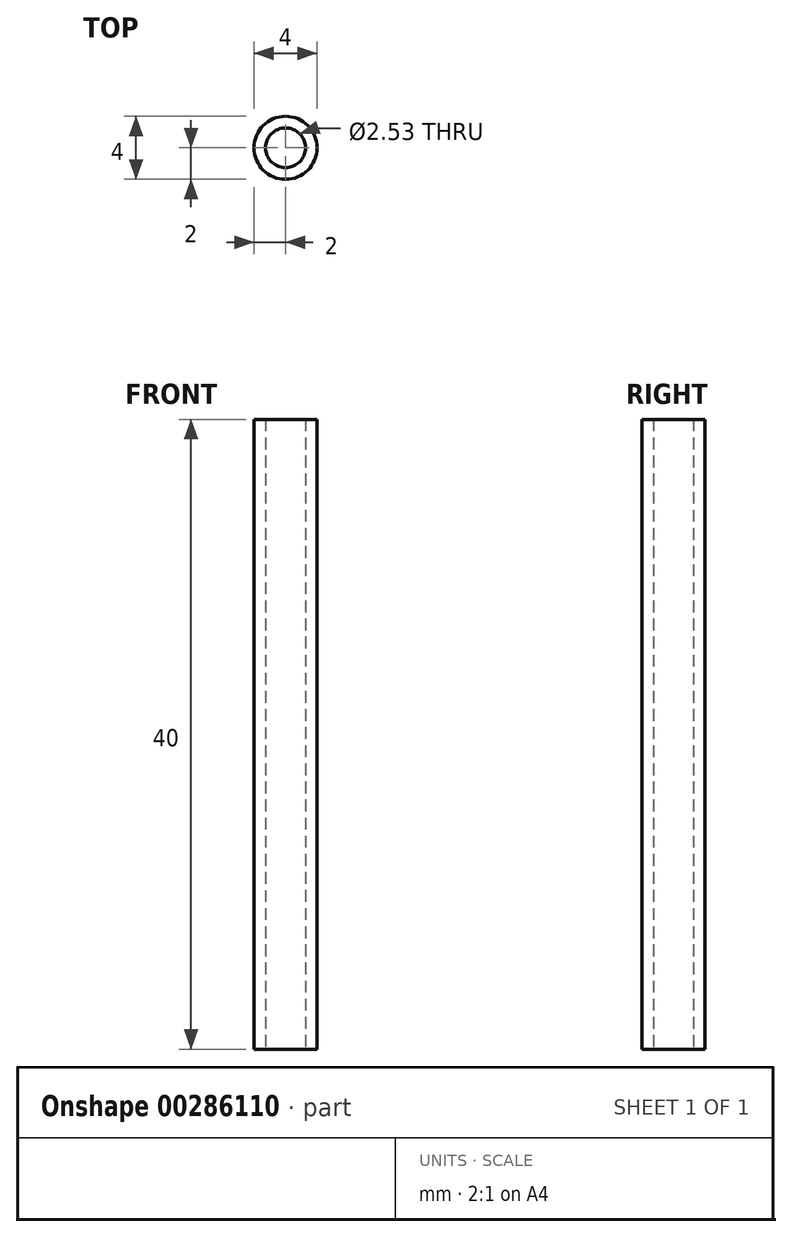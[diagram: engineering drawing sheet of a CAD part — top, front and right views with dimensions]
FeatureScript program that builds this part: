
annotation { "Feature Type Name" : "Feature", "Feature Type Description" : "" }
export const myFeature = defineFeature(function(context is Context, id is Id, definition is map)
    precondition{}
    {
        {
            var Q0;
            Q0=qCreatedBy(makeId("Top.planeOp"),FACE);
            var sketch = newSketch(context, id + "F0", { "sketchPlane" : qUnion([Q0])});
            skCircle(sketch, "E0", {"center": v(0, 0) * mm, "radius": 2 * mm});
            skSolve(sketch);
        }
        {
            var Q0;
            Q0=qSketchRegion(id+"F0",true);
            extrude(context, id + "F2", {"entities" : qUnion([Q0]), "depth" : 40 * mm});
        }
        {
            var Q0;
            Q0=makeQuery(id+"F2.opExtrude","CAP_FACE",FACE,{"disambiguationData":[OSD([sQuery(id+"F0.wireOp",EDGE,"E0")])],"isStart":true});
            var sketch = newSketch(context, id + "F3", { "sketchPlane" : qUnion([Q0])});
            skCircle(sketch, "E1", {"center": v(0, 0) * mm, "radius": 1.26 * mm});
            skSolve(sketch);
        }
        {
            var Q0;
            Q0=qSketchRegion(id+"F3",true);
            extrude(context, id + "F1", {"entities" : qUnion([Q0]), "operationType" : NewBodyOperationType.REMOVE, "endBound" : BoundingType.THROUGH_ALL, "oppositeDirection" : true, "depth" : 25 * mm});
        }
    });
